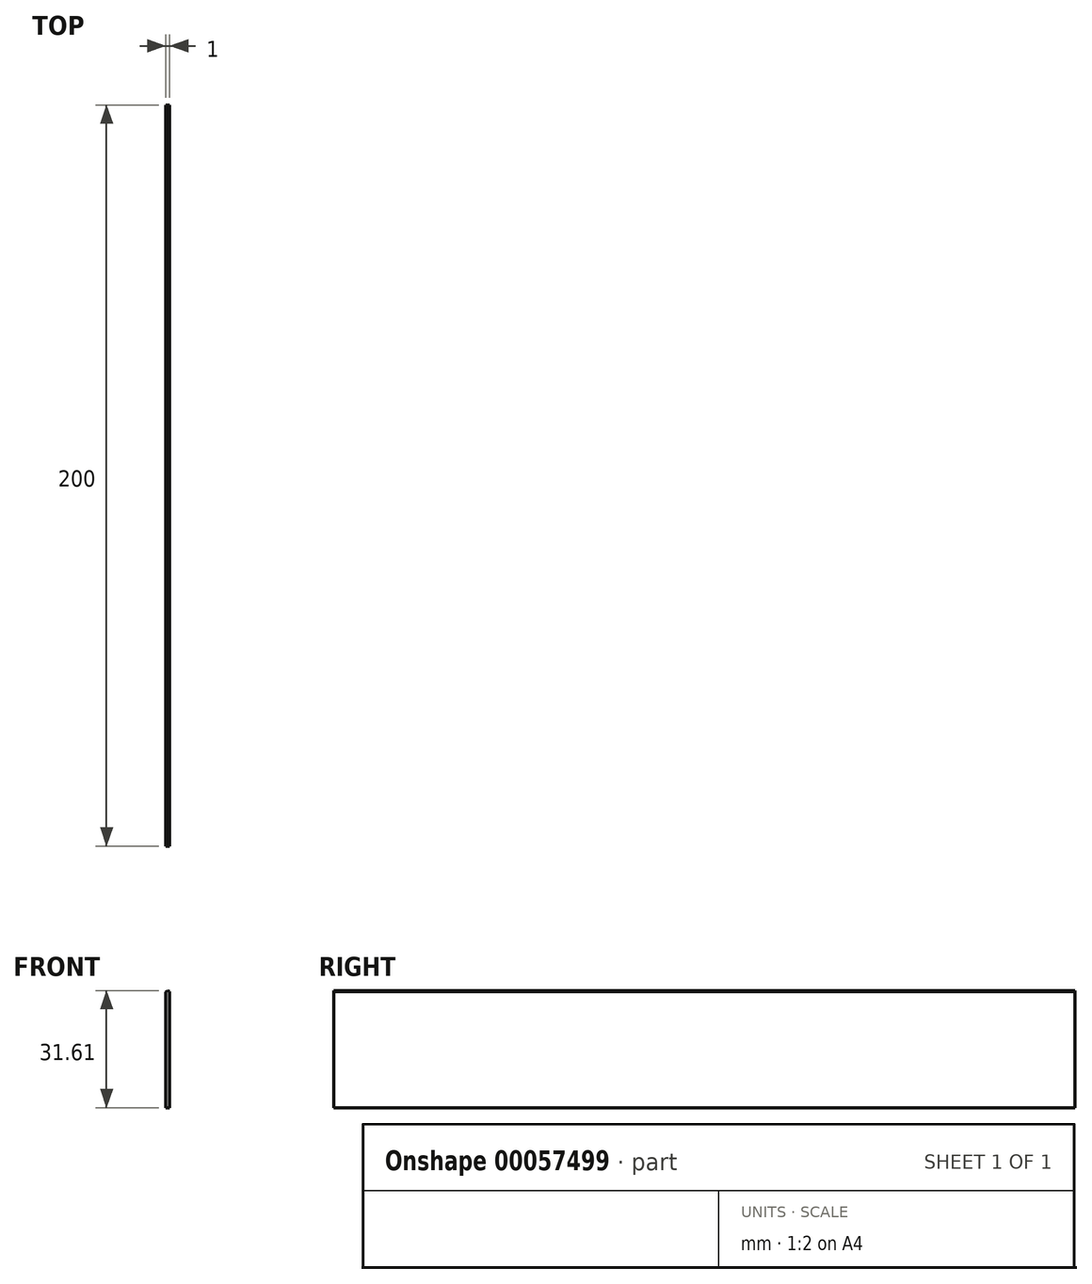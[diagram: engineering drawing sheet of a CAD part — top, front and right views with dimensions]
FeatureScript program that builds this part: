
annotation { "Feature Type Name" : "Feature", "Feature Type Description" : "" }
export const myFeature = defineFeature(function(context is Context, id is Id, definition is map)
    precondition{}
    {
        {
            var Q0;
            Q0=qCreatedBy(makeId("Front.planeOp"),FACE);
            var sketch = newSketch(context, id + "F0", { "sketchPlane" : qUnion([Q0])});
            skLineSegment(sketch, "E0", {"start": v(0, 27.37) * mm, "end": v(0, -4.65) * mm});
            skLineSegment(sketch, "E1.0", {"start": v(-1, 27.37) * mm, "end": v(-1, -4.65) * mm});
            skLineSegment(sketch, "E2", {"start": v(0, 27.37) * mm, "end": v(-1, 26.55) * mm});
            skLineSegment(sketch, "E3", {"start": v(0, -4.65) * mm, "end": v(-1, -4.65) * mm});
            skLineSegment(sketch, "E4", {"start": v(0, 26.62) * mm, "end": v(-0.5, 26.96) * mm});
            skSolve(sketch);
        }
        {
            var Q0;
            {var subQ0=sQuery(id+"F0.wireOp",EDGE,"E3");Q0=makeQuery(id+"F0.imprint","IMPRINT",FACE,{"disambiguationData":[TD([[makeQuery(id+"F0.imprint","IMPRINT",EDGE,{"derivedFrom":subQ0}),-1.0]])]});}
            extrude(context, id + "F1", {"entities" : qUnion([Q0]), "depth" : 200 * mm});
        }
    });
